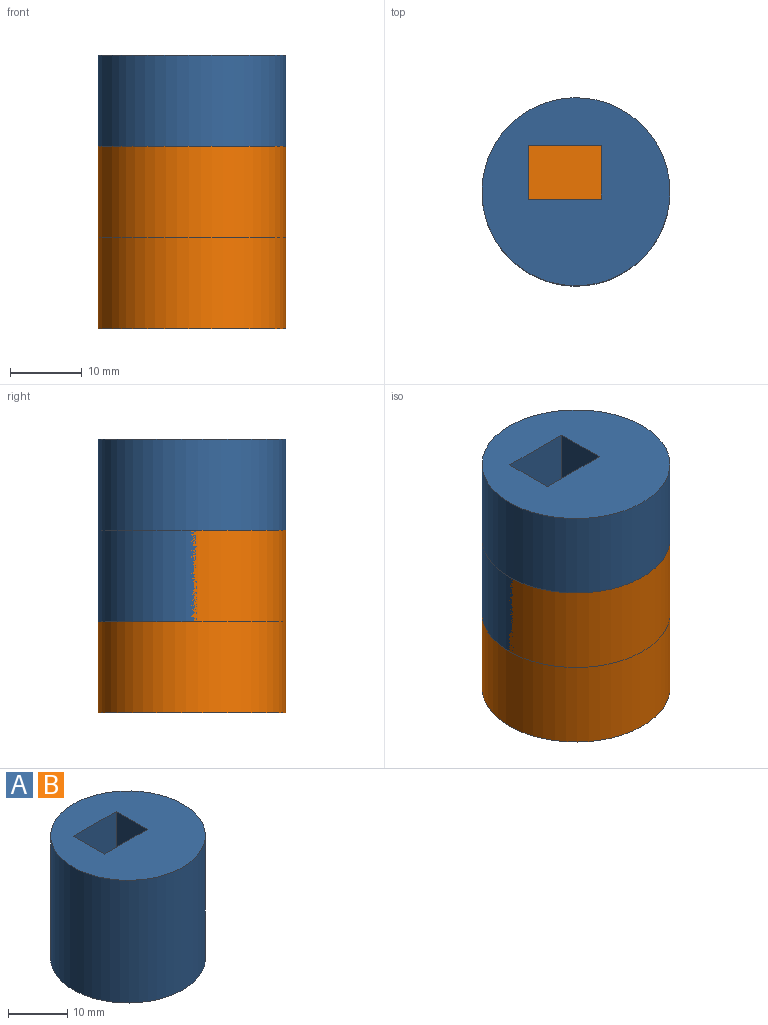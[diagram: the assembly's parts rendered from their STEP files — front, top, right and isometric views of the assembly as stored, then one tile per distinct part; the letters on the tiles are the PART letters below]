
ASSEMBLY  parts=2 mates=1
PART A: 8 faces, bbox 26.2x26.2x25.4 mm
  f0: plane 26.17x26.17mm, normal (0,0,1), area 462.4mm2, adj f1,f3,f4,f5,f6
  f1: cylinder r=13.09mm len=26.17mm, axis (0,0,-1), area 2088.4mm2, adj f0,f2
  f2: plane 26.17x26.17mm, normal (0,0,-1), area 537.9mm2, adj f1
  f3: plane 12.7x10.2mm, normal (0,-1,0), area 129.5mm2, adj f0,f4,f6,f7
  f4: plane 12.7x7.41mm, normal (1,0,0), area 94.1mm2, adj f0,f3,f5,f7
  f5: plane 12.7x10.2mm, normal (0,1,0), area 129.5mm2, adj f0,f4,f6,f7
  f6: plane 12.7x7.41mm, normal (-1,0,0), area 94.1mm2, adj f0,f3,f5,f7
  f7: plane 10.2x7.41mm, normal (0,0,1), area 75.6mm2, adj f3,f4,f5,f6
PART B: same geometry as A
PLACE A t=(-18.96,26.36,-23.53)mm
PLACE B rot(axis=(1,0,0),180deg) t=(-18.96,13.55,-10.83)mm
MATE fastened B.f1 <-> A.f1  axis (0,0,1) through (25.27,19.95,-10.83)mm
